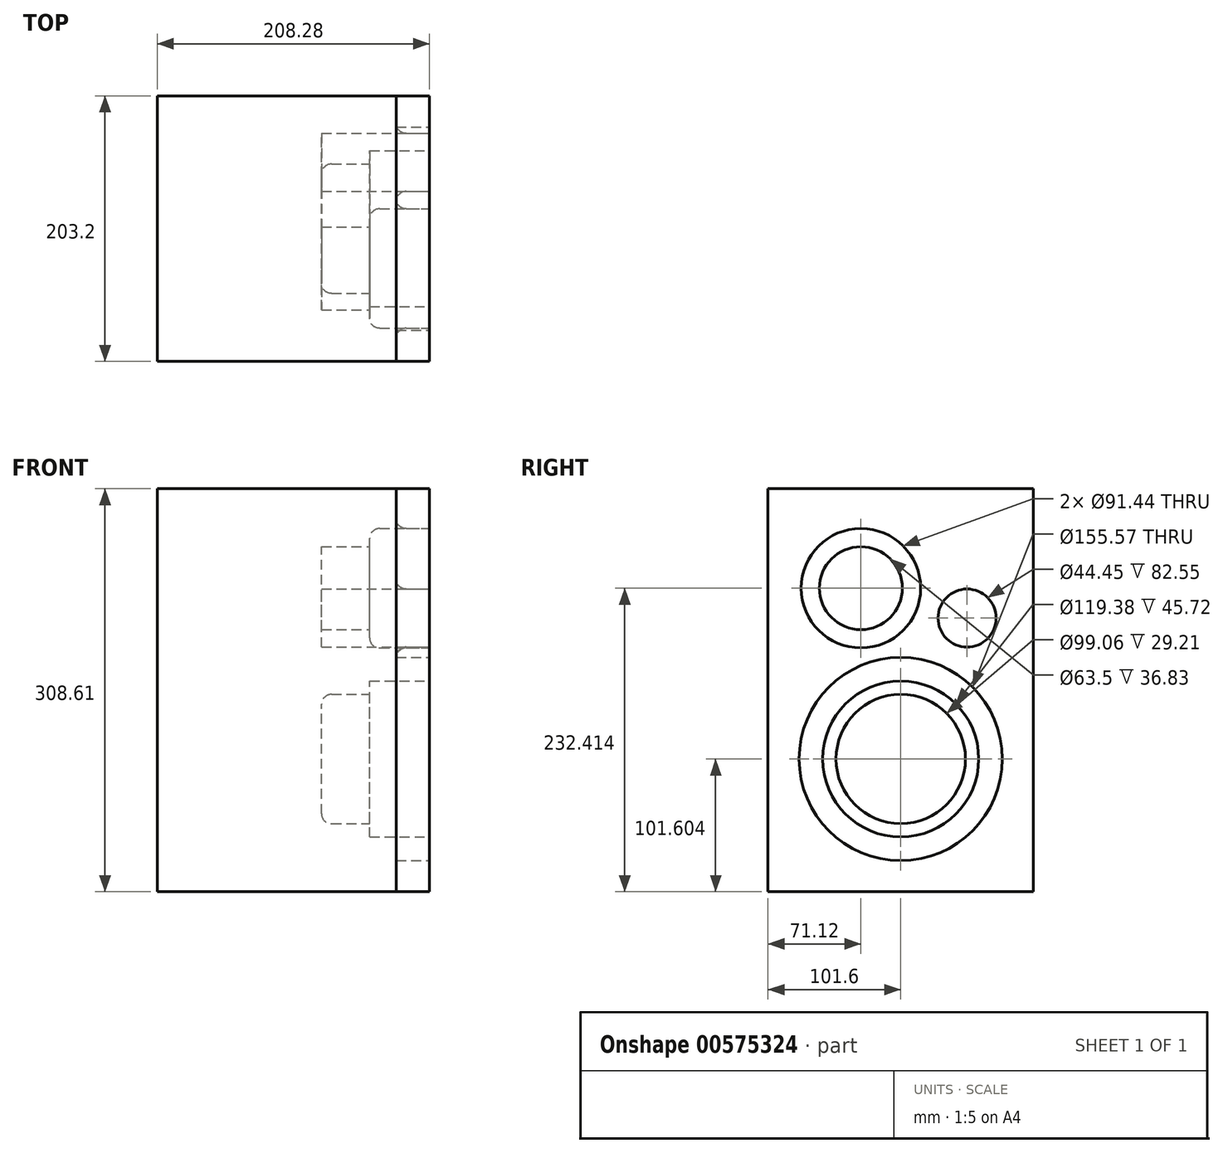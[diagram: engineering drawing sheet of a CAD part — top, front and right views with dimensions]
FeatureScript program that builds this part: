
annotation { "Feature Type Name" : "Feature", "Feature Type Description" : "" }
export const myFeature = defineFeature(function(context is Context, id is Id, definition is map)
    precondition{}
    {
        {
            var Q0;
            Q0=qCreatedBy(makeId("Front.planeOp"),FACE);
            var sketch = newSketch(context, id + "F0", { "sketchPlane" : qUnion([Q0])});
            skLineSegment(sketch, "E0.bottom", {"start": v(-101.6, 151.3) * mm, "end": v(101.6, 151.3) * mm});
            skLineSegment(sketch, "E0.top", {"start": v(-101.6, -157.3) * mm, "end": v(101.6, -157.3) * mm});
            skLineSegment(sketch, "E0.left", {"start": v(-101.6, 151.3) * mm, "end": v(-101.6, -157.3) * mm});
            skLineSegment(sketch, "E0.right", {"start": v(101.6, 151.3) * mm, "end": v(101.6, -157.3) * mm});
            skCircle(sketch, "E1", {"center": v(-30.48, 75.1) * mm, "radius": 31.75 * mm});
            skCircle(sketch, "E2", {"center": v(50.8, 52.24) * mm, "radius": 22.23 * mm});
            skCircle(sketch, "E3", {"center": v(-30.48, 75.1) * mm, "radius": 45.72 * mm});
            skCircle(sketch, "E4", {"center": v(0, -55.7) * mm, "radius": 49.53 * mm});
            skCircle(sketch, "E5", {"center": v(0, -55.7) * mm, "radius": 59.7 * mm});
            skCircle(sketch, "E6", {"center": v(0, -55.7) * mm, "radius": 77.79 * mm});
            skSolve(sketch);
        }
        {
            var Q0;
            Q0=makeQuery(id+"F0.imprint","IMPRINT",FACE,{"disambiguationData":[TD([[makeQuery(id+"F0.imprint","IMPRINT",EDGE,{"derivedFrom":sQuery(id+"F0.wireOp",EDGE,"E0.bottom")}),-1.0]])]});
            var Q1;
            Q1=makeQuery(id+"F0.imprint","IMPRINT",FACE,{"disambiguationData":[TD([[makeQuery(id+"F0.imprint","IMPRINT",EDGE,{"derivedFrom":sQuery(id+"F0.wireOp",EDGE,"E5")}),-1.0]])]});
            var Q2;
            Q2=makeQuery(id+"F0.imprint","IMPRINT",FACE,{"disambiguationData":[TD([[makeQuery(id+"F0.imprint","IMPRINT",EDGE,{"derivedFrom":sQuery(id+"F0.wireOp",EDGE,"E2")}),1.0]])]});
            var Q3;
            Q3=makeQuery(id+"F0.imprint","IMPRINT",FACE,{"disambiguationData":[TD([[makeQuery(id+"F0.imprint","IMPRINT",EDGE,{"derivedFrom":sQuery(id+"F0.wireOp",EDGE,"E1")}),1.0]])]});
            var Q4;
            Q4=makeQuery(id+"F0.imprint","IMPRINT",FACE,{"disambiguationData":[TD([[makeQuery(id+"F0.imprint","IMPRINT",EDGE,{"derivedFrom":sQuery(id+"F0.wireOp",EDGE,"E1")}),-1.0]])]});
            var Q5;
            Q5=makeQuery(id+"F0.imprint","IMPRINT",FACE,{"disambiguationData":[TD([[makeQuery(id+"F0.imprint","IMPRINT",EDGE,{"derivedFrom":sQuery(id+"F0.wireOp",EDGE,"E4")}),1.0]])]});
            var Q6;
            Q6=makeQuery(id+"F0.imprint","IMPRINT",FACE,{"disambiguationData":[TD([[makeQuery(id+"F0.imprint","IMPRINT",EDGE,{"derivedFrom":sQuery(id+"F0.wireOp",EDGE,"E4")}),-1.0]])]});
            extrude(context, id + "F1", {"entities" : qUnion([Q0, Q1, Q2, Q3, Q4, Q5, Q6]), "oppositeDirection" : true, "depth" : 208.28 * mm, "offsetDistance" : 25.4 * mm});
        }
        {
            var Q0;
            Q0 = qSketchRegion(id + "F0", true);
            extrude(context, id + "F2", {"entities" : qUnion([Q0]), "oppositeDirection" : true, "depth" : 25.4 * mm, "offsetDistance" : 25.4 * mm});
        }
        {
            var Q0;
            Q0=makeQuery(id+"F0.imprint","IMPRINT",FACE,{"disambiguationData":[TD([[makeQuery(id+"F0.imprint","IMPRINT",EDGE,{"derivedFrom":sQuery(id+"F0.wireOp",EDGE,"E1")}),1.0]])]});
            var Q1;
            Q1=makeQuery(id+"F0.imprint","IMPRINT",FACE,{"disambiguationData":[TD([[makeQuery(id+"F0.imprint","IMPRINT",EDGE,{"derivedFrom":sQuery(id+"F0.wireOp",EDGE,"E2")}),1.0]])]});
            var Q2;
            Q2=makeQuery(id+"F0.imprint","IMPRINT",FACE,{"disambiguationData":[TD([[makeQuery(id+"F0.imprint","IMPRINT",EDGE,{"derivedFrom":sQuery(id+"F0.wireOp",EDGE,"E4")}),1.0]])]});
            extrude(context, id + "F3", {"entities" : qUnion([Q0, Q1, Q2]), "operationType" : NewBodyOperationType.REMOVE, "oppositeDirection" : true, "depth" : 82.55 * mm, "offsetDistance" : 25.4 * mm});
        }
        {
            var Q0;
            Q0=makeQuery(id+"F0.imprint","IMPRINT",FACE,{"disambiguationData":[TD([[makeQuery(id+"F0.imprint","IMPRINT",EDGE,{"derivedFrom":sQuery(id+"F0.wireOp",EDGE,"E1")}),-1.0]])]});
            var Q1;
            Q1=makeQuery(id+"F0.imprint","IMPRINT",FACE,{"disambiguationData":[TD([[makeQuery(id+"F0.imprint","IMPRINT",EDGE,{"derivedFrom":sQuery(id+"F0.wireOp",EDGE,"E4")}),-1.0]])]});
            extrude(context, id + "F4", {"entities" : qUnion([Q0, Q1]), "operationType" : NewBodyOperationType.REMOVE, "oppositeDirection" : true, "depth" : 45.72 * mm, "offsetDistance" : 25.4 * mm});
        }
        {
            var Q0;
            Q0=makeQuery(id+"F4.boolean.opBoolean","COPY",EDGE,{"derivedFrom":makeQuery(id+"F4.opExtrude","CAP_EDGE",EDGE,{"disambiguationData":[OSD([sQuery(id+"F0.wireOp",EDGE,"E3")])],"isStart":true})});
            var Q1;
            Q1=makeQuery(id+"F3.boolean.opBoolean","COPY",EDGE,{"derivedFrom":makeQuery(id+"F3.opExtrude","CAP_EDGE",EDGE,{"disambiguationData":[OSD([sQuery(id+"F0.wireOp",EDGE,"E2")])],"isStart":true})});
            var Q2;
            Q2=makeQuery(id+"F4.boolean.opBoolean","COPY",EDGE,{"derivedFrom":makeQuery(id+"F4.opExtrude","CAP_EDGE",EDGE,{"disambiguationData":[OSD([sQuery(id+"F0.wireOp",EDGE,"E5")])],"isStart":true})});
            var Q3;
            Q3=makeQuery(id+"F4.boolean.opBoolean","COPY",EDGE,{"derivedFrom":makeQuery(id+"F4.opExtrude","CAP_EDGE",EDGE,{"disambiguationData":[OSD([sQuery(id+"F0.wireOp",EDGE,"E4")])],"isStart":false})});
            var Q4;
            Q4=makeQuery(id+"F3.boolean.opBoolean","COPY",EDGE,{"derivedFrom":makeQuery(id+"F3.opExtrude","CAP_EDGE",EDGE,{"disambiguationData":[OSD([sQuery(id+"F0.wireOp",EDGE,"E4")])],"isStart":false})});
            var Q5;
            Q5=makeQuery(id+"F4.boolean.opBoolean","COPY",EDGE,{"derivedFrom":makeQuery(id+"F4.opExtrude","CAP_EDGE",EDGE,{"disambiguationData":[OSD([sQuery(id+"F0.wireOp",EDGE,"E3")])],"isStart":false})});
            var Q6;
            Q6=makeQuery(id+"F2.opExtrude","CAP_EDGE",EDGE,{"disambiguationData":[OSD([sQuery(id+"F0.wireOp",EDGE,"E3")])],"isStart":false});
            var Q7;
            Q7=makeQuery(id+"F2.opExtrude","CAP_EDGE",EDGE,{"disambiguationData":[OSD([sQuery(id+"F0.wireOp",EDGE,"E2")])],"isStart":false});
            fillet(context, id + "F5", {"entities" : qUnion([Q0, Q1, Q2, Q3, Q4, Q5, Q6, Q7]), "radius" : 7.62 * mm, "tangentPropagation" : true, "allowEdgeOverflow" : false});
        }
        {
            var Q0;
            Q0=makeQuery(id+"F1.opExtrude","SWEPT_BODY",BODY,{"disambiguationData":[OSD([sQuery(id+"F0.wireOp",EDGE,"E0.bottom"),sQuery(id+"F0.wireOp",EDGE,"E0.top"),sQuery(id+"F0.wireOp",EDGE,"E0.left"),sQuery(id+"F0.wireOp",EDGE,"E0.right")])]});
            var Q1;
            Q1=makeQuery(id+"F2.opExtrude","SWEPT_BODY",BODY,{"disambiguationData":[OSD([sQuery(id+"F0.wireOp",EDGE,"E0.bottom"),sQuery(id+"F0.wireOp",EDGE,"E0.top"),sQuery(id+"F0.wireOp",EDGE,"E0.left"),sQuery(id+"F0.wireOp",EDGE,"E0.right"),sQuery(id+"F0.wireOp",EDGE,"E2"),sQuery(id+"F0.wireOp",EDGE,"E3"),sQuery(id+"F0.wireOp",EDGE,"E6")])]});
            var Q2;
            Q2=makeQuery(id+"F1.opExtrude","CAP_EDGE",EDGE,{"disambiguationData":[OSD([sQuery(id+"F0.wireOp",EDGE,"E0.right")])],"isStart":true});
            transform(context, id + "F6", {"entities" : qUnion([Q0, Q1]), "transformType" : TransformType.ROTATION, "transformAxis" : qUnion([Q2]), "angle" : 90 * degree, "oppositeDirection" : true, "makeCopy" : false});
        }
    });
